# Revit family: BEG-97003
name_source: partatom
category: Dispositifs d'éclairage
revit_build: Autodesk Revit 2015 (Build: 20140606_1530(x64)
units: mm (PartAtom-declared; Revit-internal decimal feet)

## types (1)
- BEG-97003
    Artikel-Nummer = 97003
    Ausgabetyp = Schalten
    Code d'assemblage = D5010200
    Commentaires du type = RC-plus next 280-weiß  BEG Luxomat Bewegungsmelder
    Elévation par défaut = 250 cm
    Fabricant = B.E.G
    IP = 54
    Image du type = 97003.jpg
    Klasse = 2
    Marke = LUXOMAT
    Max Montagehöhe empfohlen = 400 cm
    Modèle = RC-plus next 280, weiß
    Montagehöhe max = 400 cm
    Montge Anleitung = Aufputz und Deckenanbau Version
    Relais = 16A
    SPANNUNG = 110-240 V AC
    Schaltleistung Kanal Cos ɸ =0,5 = 1500W
    Schaltleistung Kanal Cos ɸ =1 = 3000W
    Schaltleistung Kanal LED = 300W
    Typische Leistungsaufnahme = 0.57W
    URL = http://www.luxomat.com
    Umgebungstemperatur = -25°C bis +50°C

## geometry (parser evidence)
native form markers: Extrusion x2
no freeform markers — native parametric forms only
